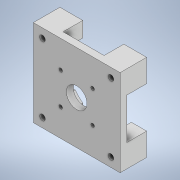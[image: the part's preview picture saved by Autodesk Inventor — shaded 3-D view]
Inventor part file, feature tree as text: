
AUTODESK INVENTOR PART (.ipt)
format: ipt  version: 2022.2 (Build 262287030, 287C)  size: 185,344 bytes
history: native  units: in
note: dims shown in document units (in); Inventor stores cm internally (conversion verified against a paired STEP export)
features: sketch x7, extrude x4, hole x3, projected_geometry x1
ambient origin geometry x8: Origin, YZ Plane, XZ Plane, XY Plane, X Axis, Y Axis, Z Axis, Center Point
bodies: Solid1 (feature_tree)
feature tree (15):
  extrude  "Extrusion1"  Depth=1.4961in
  sketch  "Sketch4"  dims[d2=0.3543in d3=0.4583in d4=0.0in]
  extrude  "Extrusion2"  Depth=0.4583in TaperAngle=0.0deg
  extrude  "Extrusion3"  Depth=0.8858in
  extrude  "Extrusion4"  Depth=0.3402in TaperAngle=0.0deg
  hole  "Hole1"  [1 undecoded]
  hole  "Hole2"  [1 undecoded]
  hole  "Hole3"  [1 undecoded]
  sketch  "Sketch1"  dims[d0=1.4961in d1=1.4961in]
  sketch  "Sketch5"  dims[d17=0.8858in d18=0.8858in]
  sketch  "Sketch6"  dims[d19=1.2in d20=0.3402in d21=0.0in]
  sketch  "Sketch7"  dims[d22=0.3937in d23=0.3937in]
  sketch  "Sketch8"  dims[d24=0.0in d25=0.0in d26=0.3937in]
  projected_geometry  "Projected Loop1"
  sketch  "Sketch9"  dims[d27=0.3937in d28=0.0in d29=0.0in d30=0.5906in d31=0.5906in d32=0.7874in d34=1.1811in d35=0.7874in d37=1.1811in d40=0.0787in d41=0.1575in d42=0.1476in d43=0.0984in d44=90.0deg d45=0.1575in d46=0.0in d47=0.2756in d48=0.2756in d49=0.7874in d51=0.5512in d52=0.7874in d54=0.5512in d57=0.0617in d58=0.1575in d59=0.1476in d60=0.0984in d61=90.0deg d62=0.3937in d63=0.0in d64=0.0984in d65=0.1181in d66=0.1476in d67=0.0984in d68=90.0deg d69=0.1181in d70=0.0in d12=0.0in d13=0.0in d14=0.0in d15=0.0in d16=0.0in d71=0.2953in d72=0.8108in d73=0.0246in d74=0.2953in d75=0.1476in]
note: 3 required parameter values undecoded (feature->parameter linkage not recoverable at this tier; creation-order binding heuristic only, values carry confidence <= 0.55)
